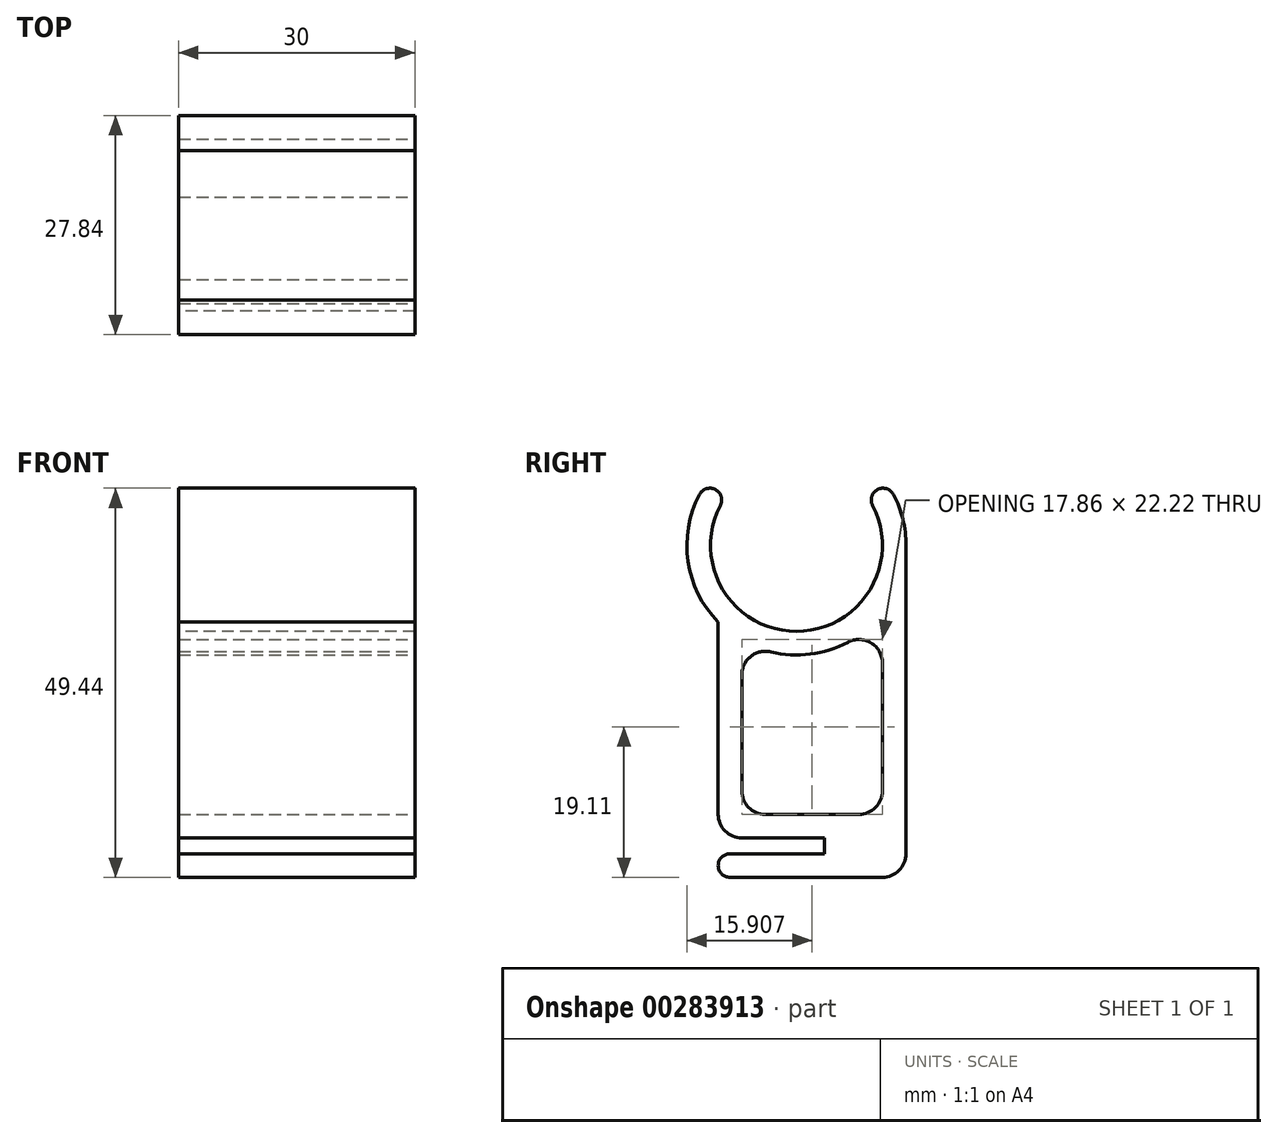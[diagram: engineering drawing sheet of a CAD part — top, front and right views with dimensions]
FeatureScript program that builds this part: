
annotation { "Feature Type Name" : "Feature", "Feature Type Description" : "" }
export const myFeature = defineFeature(function(context is Context, id is Id, definition is map)
    precondition{}
    {
        {
            var Q0;
            Q0=qCreatedBy(makeId("Right.planeOp"),FACE);
            var sketch = newSketch(context, id + "F0", { "sketchPlane" : qUnion([Q0])});
            skCircle(sketch, "E0", {"center": v(0, 0) * mm, "radius": 10.92 * mm, "construction": true});
            skLineSegment(sketch, "E1", {"start": v(0, 0) * mm, "end": v(0, -86) * mm, "construction": true});
            skPoint(sketch, "E2", {"position": v(0, -44.75) * mm});
            skPoint(sketch, "E3", {"position": v(0, -40) * mm});
            skArc(sketch, "E4", {"start": v(9.67, 5.07) * mm, "mid": v(0, -10.92) * mm, "end": v(-9.67, 5.07) * mm});
            skLineSegment(sketch, "E5", {"start": v(0, 0) * mm, "end": v(0, 10.92) * mm, "construction": true});
            skLineSegment(sketch, "E6", {"start": v(0, 7.27) * mm, "end": v(33.13, 7.27) * mm, "construction": true});
            skArc(sketch, "E7", {"start": v(-12.32, 6.47) * mm, "mid": v(0, -13.92) * mm, "end": v(12.32, 6.47) * mm});
            skArc(sketch, "E8", {"start": v(-9.67, 5.07) * mm, "mid": v(-10.3, 7.1) * mm, "end": v(-12.32, 6.47) * mm});
            skArc(sketch, "E9.MirrorCS", {"start": v(9.67, 5.07) * mm, "mid": v(10.3, 7.1) * mm, "end": v(12.32, 6.47) * mm});
            skSolve(sketch);
        }
        {
            var Q0;
            Q0=qSketchRegion(id+"F0",true);
            extrude(context, id + "F1", {"entities" : qUnion([Q0]), "endBound" : BoundingType.SYMMETRIC, "depth" : 30 * mm});
        }
        {
            var Q0;
            Q0=makeQuery(id+"F1.opExtrude","CAP_FACE",FACE,{"disambiguationData":[OSD([sQuery(id+"F0.wireOp",EDGE,"E4"),sQuery(id+"F0.wireOp",EDGE,"E7"),sQuery(id+"F0.wireOp",EDGE,"E8"),sQuery(id+"F0.wireOp",EDGE,"E9.MirrorCS")])],"isStart":false});
            var sketch = newSketch(context, id + "F2", { "sketchPlane" : qUnion([Q0])});
            skLineSegment(sketch, "E10", {"start": v(0, 0) * mm, "end": v(0, -60.18) * mm, "construction": true});
            skArc(sketch, "E11.0", {"start": v(-9.94, -9.74) * mm, "mid": v(5.26, -12.89) * mm, "end": v(13.92, 0) * mm});
            skLineSegment(sketch, "E12", {"start": v(0, 0) * mm, "end": v(13.92, 0) * mm, "construction": true});
            skLineSegment(sketch, "E13", {"start": v(13.92, 0) * mm, "end": v(13.92, -42.17) * mm});
            skPoint(sketch, "E14", {"position": v(0, -37.17) * mm});
            skLineSegment(sketch, "E15", {"start": v(3.56, 0) * mm, "end": v(3.56, -61.1) * mm, "construction": true});
            skLineSegment(sketch, "E16", {"start": v(-9.94, -37.17) * mm, "end": v(3.56, -37.17) * mm});
            skLineSegment(sketch, "E17", {"start": v(-9.94, -37.17) * mm, "end": v(-9.94, -9.74) * mm});
            skLineSegment(sketch, "E18", {"start": v(3.56, -37.17) * mm, "end": v(3.56, -39.17) * mm});
            skLineSegment(sketch, "E19", {"start": v(3.56, -39.17) * mm, "end": v(-9.94, -39.17) * mm});
            skLineSegment(sketch, "E20", {"start": v(-9.94, -39.17) * mm, "end": v(-9.94, -42.17) * mm});
            skLineSegment(sketch, "E21", {"start": v(-9.94, -42.17) * mm, "end": v(13.92, -42.17) * mm});
            skPoint(sketch, "E22.orphan", {"position": v(-12.32, 6.47) * mm});
            skPoint(sketch, "E23.orphan", {"position": v(12.32, 6.47) * mm});
            skSolve(sketch);
        }
        {
            var Q0;
            Q0 = qSketchRegion(id + "F2", true);
            var Q1;
            Q1=makeQuery(id+"F1.opExtrude","CAP_FACE",FACE,{"disambiguationData":[OSD([sQuery(id+"F0.wireOp",EDGE,"E4"),sQuery(id+"F0.wireOp",EDGE,"E7"),sQuery(id+"F0.wireOp",EDGE,"E8"),sQuery(id+"F0.wireOp",EDGE,"E9.MirrorCS")])],"isStart":true});
            extrude(context, id + "F3", {"entities" : qUnion([Q0]), "operationType" : NewBodyOperationType.ADD, "endBound" : BoundingType.UP_TO_SURFACE, "oppositeDirection" : true, "endBoundEntityFace" : qUnion([Q1]), "depth" : 25 * mm});
        }
        {
            var Q0;
            Q0=makeQuery(id+"F3.opExtrude","SWEPT_EDGE",EDGE,{"disambiguationData":[OSD([sQuery(id+"F2.wireOp",EDGE,"E19"),sQuery(id+"F2.wireOp",EDGE,"E20")])]});
            var Q1;
            Q1=makeQuery(id+"F3.opExtrude","SWEPT_EDGE",EDGE,{"disambiguationData":[OSD([sQuery(id+"F2.wireOp",EDGE,"E20"),sQuery(id+"F2.wireOp",EDGE,"E21")])]});
            fillet(context, id + "F4", {"entities" : qUnion([Q0, Q1]), "radius" : 1.5 * mm, "tangentPropagation" : true, "allowEdgeOverflow" : false});
        }
        {
            var Q0;
            Q0=makeQuery(id+"F3.boolean.opBoolean","MERGE",FACE,{"derivedFrom":[makeQuery(id+"F1.opExtrude","CAP_FACE",FACE,{"disambiguationData":[OSD([sQuery(id+"F0.wireOp",EDGE,"E4"),sQuery(id+"F0.wireOp",EDGE,"E7"),sQuery(id+"F0.wireOp",EDGE,"E8"),sQuery(id+"F0.wireOp",EDGE,"E9.MirrorCS")])],"isStart":false}),makeQuery(id+"F3.opExtrude","CAP_FACE",FACE,{"disambiguationData":[OSD([sQuery(id+"F2.wireOp",EDGE,"E11.0"),sQuery(id+"F2.wireOp",EDGE,"E13"),sQuery(id+"F2.wireOp",EDGE,"E16"),sQuery(id+"F2.wireOp",EDGE,"E17"),sQuery(id+"F2.wireOp",EDGE,"E18"),sQuery(id+"F2.wireOp",EDGE,"E19"),sQuery(id+"F2.wireOp",EDGE,"E20"),sQuery(id+"F2.wireOp",EDGE,"E21")])],"isStart":true})]});
            var sketch = newSketch(context, id + "F5", { "sketchPlane" : qUnion([Q0])});
            skArc(sketch, "E24", {"start": v(-6.94, -12.06) * mm, "mid": v(2.62, -13.67) * mm, "end": v(10.92, -8.63) * mm});
            skLineSegment(sketch, "E25", {"start": v(-6.94, -12.06) * mm, "end": v(-6.94, -34.17) * mm});
            skLineSegment(sketch, "E26", {"start": v(-6.94, -34.17) * mm, "end": v(10.92, -34.17) * mm});
            skLineSegment(sketch, "E27", {"start": v(10.92, -34.17) * mm, "end": v(10.92, -8.63) * mm});
            skSolve(sketch);
        }
        {
            var Q0;
            Q0 = qSketchRegion(id + "F5", true);
            extrude(context, id + "F6", {"entities" : qUnion([Q0]), "operationType" : NewBodyOperationType.REMOVE, "endBound" : BoundingType.THROUGH_ALL, "oppositeDirection" : true, "depth" : 25 * mm});
        }
        {
            var Q0;
            Q0=makeQuery(id+"F3.opExtrude","SWEPT_EDGE",EDGE,{"disambiguationData":[OSD([sQuery(id+"F0.wireOp",EDGE,"E7"),sQuery(id+"F2.wireOp",EDGE,"E11.0"),sQuery(id+"F2.wireOp",EDGE,"E17")])]});
            var Q1;
            Q1=makeQuery(id+"F3.opExtrude","SWEPT_EDGE",EDGE,{"disambiguationData":[OSD([sQuery(id+"F2.wireOp",EDGE,"E16"),sQuery(id+"F2.wireOp",EDGE,"E17")])]});
            var Q2;
            Q2=makeQuery(id+"F3.opExtrude","SWEPT_EDGE",EDGE,{"disambiguationData":[OSD([sQuery(id+"F2.wireOp",EDGE,"E13"),sQuery(id+"F2.wireOp",EDGE,"E21")])]});
            var Q3;
            Q3=makeQuery(id+"F6.boolean.opBoolean","COPY",EDGE,{"derivedFrom":makeQuery(id+"F6.opExtrude","SWEPT_EDGE",EDGE,{"disambiguationData":[OSD([sQuery(id+"F5.wireOp",EDGE,"E24"),sQuery(id+"F5.wireOp",EDGE,"E25")])]})});
            var Q4;
            Q4=makeQuery(id+"F6.boolean.opBoolean","COPY",EDGE,{"derivedFrom":makeQuery(id+"F6.opExtrude","SWEPT_EDGE",EDGE,{"disambiguationData":[OSD([sQuery(id+"F5.wireOp",EDGE,"E24"),sQuery(id+"F5.wireOp",EDGE,"E27")])]})});
            var Q5;
            Q5=makeQuery(id+"F6.boolean.opBoolean","COPY",EDGE,{"derivedFrom":makeQuery(id+"F6.opExtrude","SWEPT_EDGE",EDGE,{"disambiguationData":[OSD([sQuery(id+"F5.wireOp",EDGE,"E26"),sQuery(id+"F5.wireOp",EDGE,"E27")])]})});
            var Q6;
            Q6=makeQuery(id+"F6.boolean.opBoolean","COPY",EDGE,{"derivedFrom":makeQuery(id+"F6.opExtrude","SWEPT_EDGE",EDGE,{"disambiguationData":[OSD([sQuery(id+"F5.wireOp",EDGE,"E25"),sQuery(id+"F5.wireOp",EDGE,"E26")])]})});
            fillet(context, id + "F7", {"entities" : qUnion([Q0, Q1, Q2, Q3, Q4, Q5, Q6]), "radius" : 3 * mm, "tangentPropagation" : true, "allowEdgeOverflow" : false});
        }
    });
